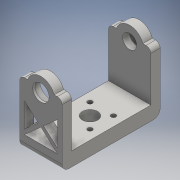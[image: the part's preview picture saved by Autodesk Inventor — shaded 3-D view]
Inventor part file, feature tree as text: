
AUTODESK INVENTOR PART (.ipt)
format: ipt  version: 2016 (Build 200138000, 138)  size: 282,112 bytes
history: native  units: mm
features: extrude x8, sketch x8, fillet x2, other x1
ambient origin geometry x8: Origin, YZ Plane, XZ Plane, XY Plane, X Axis, Y Axis, Z Axis, Center Point
bodies: Body1 (feature_tree)
feature tree (19):
  other  "ソリッド1"
  extrude  "押し出し1"  Depth=18.0mm
  extrude  "押し出し2"  Depth=41.8mm
  extrude  "押し出し3"  Depth=6.5mm
  extrude  "押し出し4"  Depth=10.0mm
  extrude  "押し出し5"  Depth=10.0mm
  extrude  "押し出し6"  Depth=2.0mm
  extrude  "押し出し7"  Depth=2.0mm
  extrude  "押し出し8"  Depth=2.0mm
  fillet  "フィレット1"  Radius=2.0mm
  fillet  "フィレット2"  Radius=6.0mm
  sketch  "スケッチ1"
  sketch  "スケッチ2"
  sketch  "スケッチ3"
  sketch  "スケッチ4"
  sketch  "スケッチ5"
  sketch  "スケッチ6"
  sketch  "スケッチ7"
  sketch  "スケッチ8"
